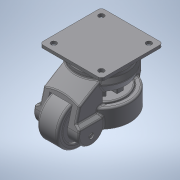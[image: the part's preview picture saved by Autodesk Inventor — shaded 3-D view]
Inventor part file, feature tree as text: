
AUTODESK INVENTOR PART (.ipt)
format: ipt  version: 2020.3 (Build 243373000, 373)  size: 1,036,800 bytes
history: native  units: in
note: dims shown in document units (in); Inventor stores cm internally (conversion verified against a paired STEP export)
features: plane x2, revolve x1, other x1, fillet x1
ambient origin geometry x8: Origin, YZ Plane, XZ Plane, XY Plane, X Axis, Y Axis, Z Axis, Center Point
bodies: Solid1 (feature_tree), Solid2 (feature_tree), Solid3 (feature_tree)
feature tree (5):
  plane  "Work Plane1"
  plane  "Work Plane2"
  revolve  "Revolve4"  [1 undecoded]
  other  "Boss-Extrude10"
  fillet  "Fillet16"  [1 undecoded]
note: 2 required parameter values undecoded (feature->parameter linkage not recoverable at this tier; creation-order binding heuristic only, values carry confidence <= 0.55)